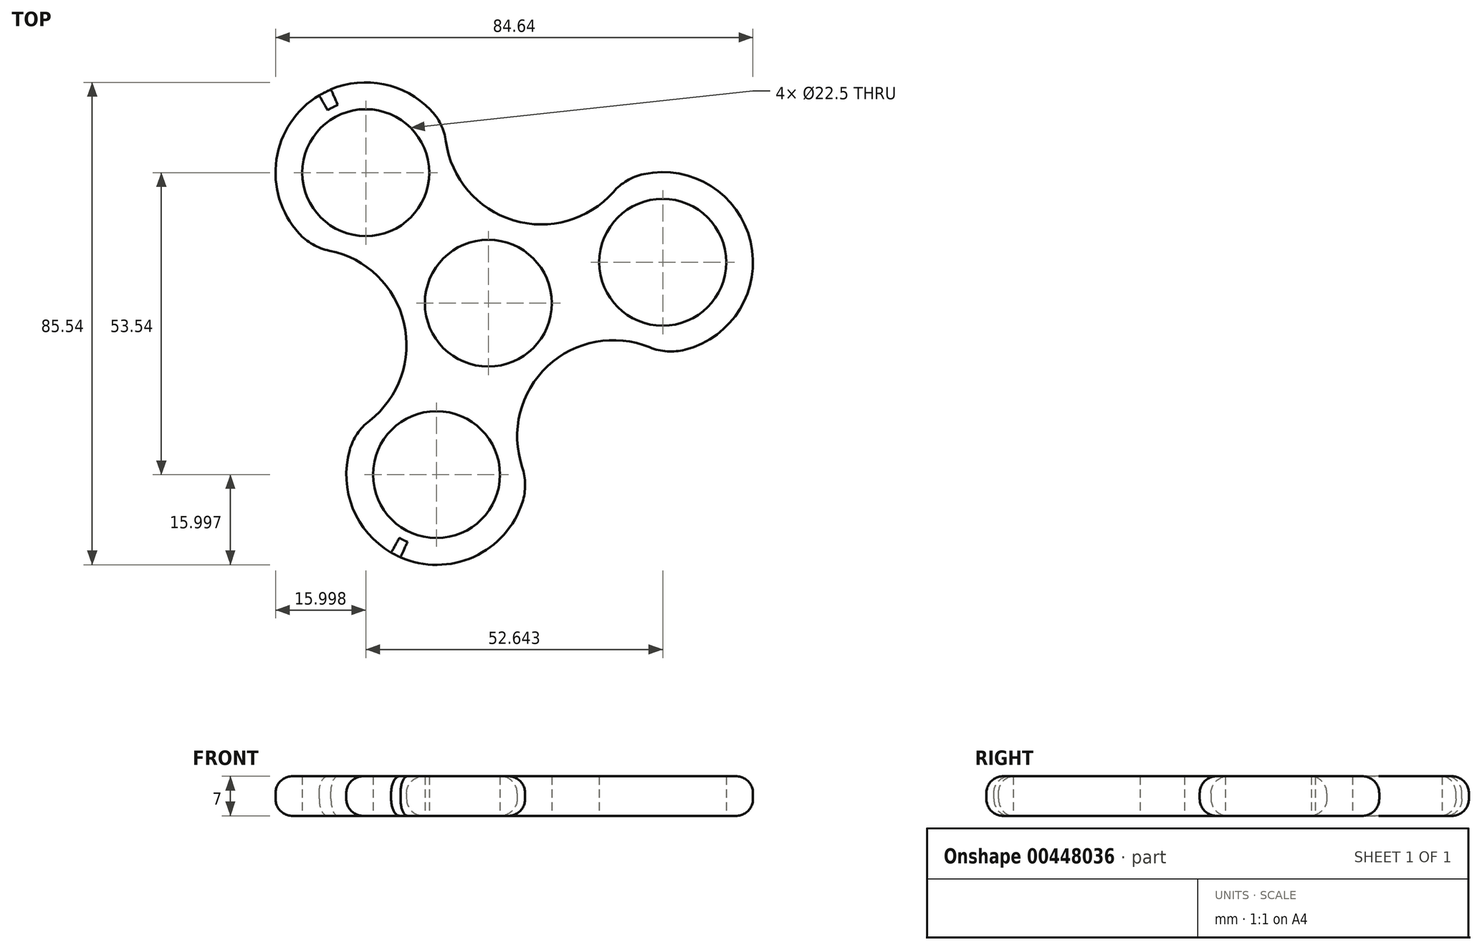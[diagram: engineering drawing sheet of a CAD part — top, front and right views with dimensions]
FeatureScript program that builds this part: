
annotation { "Feature Type Name" : "Feature", "Feature Type Description" : "" }
export const myFeature = defineFeature(function(context is Context, id is Id, definition is map)
    precondition{}
    {
        {
            var Q0;
            Q0=qCreatedBy(makeId("Top.planeOp"),FACE);
            var sketch = newSketch(context, id + "F0", { "sketchPlane" : qUnion([Q0])});
            skCircle(sketch, "E0", {"center": v(0, 0) * mm, "radius": 31.75 * mm});
            skCircle(sketch, "E1", {"center": v(30.91, 7.25) * mm, "radius": 16 * mm});
            skCircle(sketch, "E2", {"center": v(-21.73, 23.15) * mm, "radius": 16 * mm});
            skCircle(sketch, "E3", {"center": v(-9.18, -30.4) * mm, "radius": 16 * mm});
            skArc(sketch, "E4", {"start": v(-7.68, 30.8) * mm, "mid": v(4.44, 14.7) * mm, "end": v(23.45, 21.4) * mm});
            skArc(sketch, "E5", {"start": v(30.52, -8.75) * mm, "mid": v(10.5, -11.18) * mm, "end": v(6.8, -31.01) * mm});
            skArc(sketch, "E6", {"start": v(-22.84, -22.06) * mm, "mid": v(-14.95, -3.5) * mm, "end": v(-30.26, 9.6) * mm});
            skCircle(sketch, "E7", {"center": v(0, 0) * mm, "radius": 11.25 * mm});
            skCircle(sketch, "E8", {"center": v(30.91, 7.25) * mm, "radius": 11.25 * mm});
            skCircle(sketch, "E9", {"center": v(-21.73, 23.15) * mm, "radius": 11.25 * mm});
            skCircle(sketch, "E10", {"center": v(-9.18, -30.4) * mm, "radius": 11.25 * mm});
            skFitSpline(sketch, "E11", {"points": [v(46.91, 7.25) * mm, v(39.6, -18.54) * mm, v(30.52, -8.75) * mm], "startDerivative": vector(2, -70.39) * mm, "endDerivative": vector(-70.68, 26.23) * mm});
            skFitSpline(sketch, "E12", {"points": [v(-15.57, -45.06) * mm, v(-34.22, -24.14) * mm, v(-22.84, -22.06) * mm], "startDerivative": vector(-54.82, 25.3) * mm, "endDerivative": vector(33.4, 45.3) * mm});
            skFitSpline(sketch, "E13", {"points": [v(-29.99, 36.85) * mm, v(-4.27, 43.84) * mm, v(-7.68, 30.8) * mm], "startDerivative": vector(48.54, 26.45) * mm, "endDerivative": vector(14.14, -72.59) * mm});
            skSolve(sketch);
        }
        {
            var Q0;
            {var subQ0=sQuery(id+"F0.wireOp",EDGE,"E4");var subQ1=sQuery(id+"F0.wireOp",EDGE,"E2");var subQ4=makeQuery(id+"F0.imprint","INTERSECT",VERTEX,{"derivedFrom":[subQ1,subQ0]});Q0=makeQuery(id+"F0.imprint","IMPRINT",FACE,{"disambiguationData":[TD([[makeQuery(id+"F0.imprint","IMPRINT",EDGE,{"disambiguationData":[TD([[subQ4,1.0]])],"derivedFrom":subQ1}),1.0]])]});}
            var Q1;
            {var subQ1=sQuery(id+"F0.wireOp",EDGE,"E0");var subQ7=sQuery(id+"F0.wireOp",EDGE,"E9");var subQ9=makeQuery(id+"F0.imprint","INTERSECT",VERTEX,{"disambiguationData":[OD(0.0)],"derivedFrom":[subQ1,subQ7]});Q1=makeQuery(id+"F0.imprint","IMPRINT",FACE,{"disambiguationData":[TD([[makeQuery(id+"F0.imprint","IMPRINT",EDGE,{"disambiguationData":[TD([[subQ9,-1.0]])],"derivedFrom":subQ7}),-1.0]])]});}
            var Q2;
            Q2=makeQuery(id+"F0.imprint","IMPRINT",FACE,{"disambiguationData":[TD([[makeQuery(id+"F0.imprint","IMPRINT",EDGE,{"derivedFrom":sQuery(id+"F0.wireOp",EDGE,"E7")}),-1.0]])]});
            var Q3;
            {var subQ0=sQuery(id+"F0.wireOp",EDGE,"E5");var subQ1=sQuery(id+"F0.wireOp",EDGE,"E3");var subQ4=makeQuery(id+"F0.imprint","INTERSECT",VERTEX,{"derivedFrom":[subQ1,subQ0]});Q3=makeQuery(id+"F0.imprint","IMPRINT",FACE,{"disambiguationData":[TD([[makeQuery(id+"F0.imprint","IMPRINT",EDGE,{"disambiguationData":[TD([[subQ4,-1.0]])],"derivedFrom":subQ1}),1.0]])]});}
            var Q4;
            {var subQ1=sQuery(id+"F0.wireOp",EDGE,"E0");var subQ6=sQuery(id+"F0.wireOp",EDGE,"E10");var subQ7=makeQuery(id+"F0.imprint","INTERSECT",VERTEX,{"disambiguationData":[OD(0.0)],"derivedFrom":[subQ1,subQ6]});Q4=makeQuery(id+"F0.imprint","IMPRINT",FACE,{"disambiguationData":[TD([[makeQuery(id+"F0.imprint","IMPRINT",EDGE,{"disambiguationData":[TD([[subQ7,-1.0]])],"derivedFrom":subQ6}),-1.0]])]});}
            var Q5;
            {var subQ2=sQuery(id+"F0.wireOp",EDGE,"E0");var subQ6=sQuery(id+"F0.wireOp",EDGE,"E8");var subQ8=makeQuery(id+"F0.imprint","INTERSECT",VERTEX,{"disambiguationData":[OD(0.0)],"derivedFrom":[subQ2,subQ6]});Q5=makeQuery(id+"F0.imprint","IMPRINT",FACE,{"disambiguationData":[TD([[makeQuery(id+"F0.imprint","IMPRINT",EDGE,{"disambiguationData":[TD([[subQ8,1.0]])],"derivedFrom":subQ6}),-1.0]])]});}
            var Q6;
            {var subQ0=sQuery(id+"F0.wireOp",EDGE,"E4");var subQ1=sQuery(id+"F0.wireOp",EDGE,"E1");var subQ4=makeQuery(id+"F0.imprint","INTERSECT",VERTEX,{"derivedFrom":[subQ1,subQ0]});Q6=makeQuery(id+"F0.imprint","IMPRINT",FACE,{"disambiguationData":[TD([[makeQuery(id+"F0.imprint","IMPRINT",EDGE,{"disambiguationData":[TD([[subQ4,-1.0]])],"derivedFrom":subQ1}),1.0]])]});}
            var Q7;
            {var subQ0=sQuery(id+"F0.wireOp",EDGE,"ff2b849e-344e-4c15-b2b1-f3fe148f32d7");Q7=makeQuery(id+"F0.imprint","IMPRINT",FACE,{"disambiguationData":[TD([[makeQuery(id+"F0.imprint","IMPRINT",EDGE,{"derivedFrom":subQ0}),-1.0]])]});}
            var Q8;
            {var subQ0=sQuery(id+"F0.wireOp",EDGE,"E2");var subQ1=makeQuery(id+"F0.imprint","INTERSECT",VERTEX,{"disambiguationData":[OD(0.0)],"derivedFrom":[subQ0,sQuery(id+"F0.wireOp",EDGE,"E13")]});Q8=makeQuery(id+"F0.imprint","IMPRINT",FACE,{"disambiguationData":[TD([[makeQuery(id+"F0.imprint","IMPRINT",EDGE,{"disambiguationData":[TD([[subQ1,1.0]])],"derivedFrom":subQ0}),-1.0]])]});}
            var Q9;
            {var subQ0=sQuery(id+"F0.wireOp",EDGE,"E3");var subQ1=makeQuery(id+"F0.imprint","INTERSECT",VERTEX,{"disambiguationData":[OD(0.0)],"derivedFrom":[subQ0,sQuery(id+"F0.wireOp",EDGE,"E12")]});Q9=makeQuery(id+"F0.imprint","IMPRINT",FACE,{"disambiguationData":[TD([[makeQuery(id+"F0.imprint","IMPRINT",EDGE,{"disambiguationData":[TD([[subQ1,1.0]])],"derivedFrom":subQ0}),-1.0]])]});}
            var Q10;
            {var subQ0=sQuery(id+"F0.wireOp",EDGE,"0b5abbfc-5263-4152-91cc-4886121da727");var subQ1=sQuery(id+"F0.wireOp",EDGE,"E2");var subQ2=makeQuery(id+"F0.imprint","INTERSECT",VERTEX,{"disambiguationData":[OD(1.0)],"derivedFrom":[subQ1,subQ0]});Q10=makeQuery(id+"F0.imprint","IMPRINT",FACE,{"disambiguationData":[TD([[makeQuery(id+"F0.imprint","IMPRINT",EDGE,{"disambiguationData":[TD([[subQ2,-1.0]])],"derivedFrom":subQ1}),-1.0]])]});}
            var Q11;
            {var subQ0=sQuery(id+"F0.wireOp",EDGE,"0b5abbfc-5263-4152-91cc-4886121da727");var subQ1=sQuery(id+"F0.wireOp",EDGE,"E2");var subQ2=makeQuery(id+"F0.imprint","INTERSECT",VERTEX,{"disambiguationData":[OD(2.0)],"derivedFrom":[subQ1,subQ0]});Q11=makeQuery(id+"F0.imprint","IMPRINT",FACE,{"disambiguationData":[TD([[makeQuery(id+"F0.imprint","IMPRINT",EDGE,{"disambiguationData":[TD([[subQ2,-1.0]])],"derivedFrom":subQ1}),-1.0]])]});}
            extrude(context, id + "F1", {"entities" : qUnion([Q0, Q1, Q2, Q3, Q4, Q5, Q6, Q7, Q8, Q9, Q10, Q11]), "depth" : 7 * mm});
        }
        {
            var Q0;
            Q0=makeQuery(id+"F1.opExtrude","CAP_EDGE",EDGE,{"disambiguationData":[OSD([sQuery(id+"F0.wireOp",EDGE,"E5")])],"isStart":false});
            var Q1;
            Q1=makeQuery(id+"F1.opExtrude","CAP_EDGE",EDGE,{"disambiguationData":[OSD([sQuery(id+"F0.wireOp",EDGE,"E3")])],"isStart":false});
            var Q2;
            Q2=makeQuery(id+"F1.opExtrude","CAP_EDGE",EDGE,{"disambiguationData":[OSD([sQuery(id+"F0.wireOp",EDGE,"E12")])],"isStart":false});
            var Q3;
            Q3=makeQuery(id+"F1.opExtrude","CAP_EDGE",EDGE,{"disambiguationData":[OSD([sQuery(id+"F0.wireOp",EDGE,"E6")])],"isStart":false});
            var Q4;
            Q4=makeQuery(id+"F1.opExtrude","CAP_EDGE",EDGE,{"disambiguationData":[OSD([sQuery(id+"F0.wireOp",EDGE,"E2")])],"isStart":false});
            var Q5;
            Q5=makeQuery(id+"F1.opExtrude","CAP_EDGE",EDGE,{"disambiguationData":[OSD([sQuery(id+"F0.wireOp",EDGE,"E13")])],"isStart":false});
            var Q6;
            Q6=makeQuery(id+"F1.opExtrude","CAP_EDGE",EDGE,{"disambiguationData":[OSD([sQuery(id+"F0.wireOp",EDGE,"E4")])],"isStart":false});
            var Q7;
            Q7=makeQuery(id+"F1.opExtrude","CAP_EDGE",EDGE,{"disambiguationData":[OSD([sQuery(id+"F0.wireOp",EDGE,"E1")])],"isStart":false});
            var Q8;
            Q8=makeQuery(id+"F1.opExtrude","CAP_EDGE",EDGE,{"disambiguationData":[OSD([sQuery(id+"F0.wireOp",EDGE,"E11")])],"isStart":false});
            fillet(context, id + "F2", {"entities" : qUnion([Q0, Q1, Q2, Q3, Q4, Q5, Q6, Q7, Q8]), "radius" : 3 * mm, "tangentPropagation" : true, "allowEdgeOverflow" : false});
        }
        {
            var Q0;
            Q0=makeQuery(id+"F1.opExtrude","CAP_EDGE",EDGE,{"disambiguationData":[OSD([sQuery(id+"F0.wireOp",EDGE,"E3")])],"isStart":true});
            var Q1;
            Q1=makeQuery(id+"F1.opExtrude","CAP_EDGE",EDGE,{"disambiguationData":[OSD([sQuery(id+"F0.wireOp",EDGE,"E12")])],"isStart":true});
            var Q2;
            Q2=makeQuery(id+"F1.opExtrude","CAP_EDGE",EDGE,{"disambiguationData":[OSD([sQuery(id+"F0.wireOp",EDGE,"E6")])],"isStart":true});
            var Q3;
            Q3=makeQuery(id+"F1.opExtrude","CAP_EDGE",EDGE,{"disambiguationData":[OSD([sQuery(id+"F0.wireOp",EDGE,"E2")])],"isStart":true});
            var Q4;
            Q4=makeQuery(id+"F1.opExtrude","CAP_EDGE",EDGE,{"disambiguationData":[OSD([sQuery(id+"F0.wireOp",EDGE,"E13")])],"isStart":true});
            var Q5;
            Q5=makeQuery(id+"F1.opExtrude","CAP_EDGE",EDGE,{"disambiguationData":[OSD([sQuery(id+"F0.wireOp",EDGE,"E4")])],"isStart":true});
            var Q6;
            Q6=makeQuery(id+"F1.opExtrude","CAP_EDGE",EDGE,{"disambiguationData":[OSD([sQuery(id+"F0.wireOp",EDGE,"E1")])],"isStart":true});
            var Q7;
            Q7=makeQuery(id+"F1.opExtrude","CAP_EDGE",EDGE,{"disambiguationData":[OSD([sQuery(id+"F0.wireOp",EDGE,"E11")])],"isStart":true});
            var Q8;
            Q8=makeQuery(id+"F1.opExtrude","CAP_EDGE",EDGE,{"disambiguationData":[OSD([sQuery(id+"F0.wireOp",EDGE,"E5")])],"isStart":true});
            fillet(context, id + "F3", {"entities" : qUnion([Q0, Q1, Q2, Q3, Q4, Q5, Q6, Q7, Q8]), "radius" : 3 * mm, "tangentPropagation" : true, "allowEdgeOverflow" : false});
        }
        {
            var Q0;
            {var subQ0=sQuery(id+"F0.wireOp",EDGE,"E6");var subQ1=sQuery(id+"F0.wireOp",EDGE,"E2");Q0=makeQuery(id+"F2.opFillet","BLEND_EDGE",EDGE,{"blendedFrom":[makeQuery(id+"F1.opExtrude","CAP_EDGE",EDGE,{"disambiguationData":[OSD([subQ1]),TDD([makeQuery(id+"F0.imprint","IMPRINT",EDGE,{"disambiguationData":[TD([[makeQuery(id+"F0.imprint","INTERSECT",VERTEX,{"disambiguationData":[OD(0.0)],"derivedFrom":[subQ1,sQuery(id+"F0.wireOp",EDGE,"E13")]}),-1.0]])],"derivedFrom":subQ1})])],"isStart":false}),makeQuery(id+"F1.opExtrude","CAP_EDGE",EDGE,{"disambiguationData":[OSD([subQ0])],"isStart":false})],"blendedInto":[]});}
            var Q1;
            {var subQ0=sQuery(id+"F0.wireOp",EDGE,"E6");var subQ1=sQuery(id+"F0.wireOp",EDGE,"E2");Q1=makeQuery(id+"F3.opFillet","BLEND_EDGE",EDGE,{"blendedFrom":[makeQuery(id+"F1.opExtrude","CAP_EDGE",EDGE,{"disambiguationData":[OSD([subQ1]),TDD([makeQuery(id+"F0.imprint","IMPRINT",EDGE,{"disambiguationData":[TD([[makeQuery(id+"F0.imprint","INTERSECT",VERTEX,{"disambiguationData":[OD(0.0)],"derivedFrom":[subQ1,sQuery(id+"F0.wireOp",EDGE,"E13")]}),-1.0]])],"derivedFrom":subQ1})])],"isStart":true}),makeQuery(id+"F1.opExtrude","CAP_EDGE",EDGE,{"disambiguationData":[OSD([subQ0])],"isStart":true})],"blendedInto":[]});}
            var Q2;
            Q2=makeQuery(id+"F1.opExtrude","SWEPT_EDGE",EDGE,{"disambiguationData":[OSD([sQuery(id+"F0.wireOp",EDGE,"E0"),sQuery(id+"F0.wireOp",EDGE,"E2"),sQuery(id+"F0.wireOp",EDGE,"E6")])]});
            var Q3;
            {var subQ0=sQuery(id+"F0.wireOp",EDGE,"E4");var subQ1=sQuery(id+"F0.wireOp",EDGE,"E13");var subQ2=sQuery(id+"F0.wireOp",EDGE,"E2");Q3=makeQuery(id+"F2.opFillet","BLEND_EDGE",EDGE,{"blendedFrom":[makeQuery(id+"F1.opExtrude","CAP_EDGE",EDGE,{"disambiguationData":[OSD([subQ2]),TDD([makeQuery(id+"F0.imprint","IMPRINT",EDGE,{"disambiguationData":[TD([[makeQuery(id+"F0.imprint","INTERSECT",VERTEX,{"disambiguationData":[OD(1.0)],"derivedFrom":[subQ2,subQ1]}),1.0]])],"derivedFrom":subQ2})])],"isStart":false}),makeQuery(id+"F1.opExtrude","CAP_EDGE",EDGE,{"disambiguationData":[OSD([subQ0])],"isStart":false})],"blendedInto":[]});}
            var Q4;
            Q4=makeQuery(id+"F1.opExtrude","SWEPT_EDGE",EDGE,{"disambiguationData":[OSD([sQuery(id+"F0.wireOp",EDGE,"E0"),sQuery(id+"F0.wireOp",EDGE,"E2"),sQuery(id+"F0.wireOp",EDGE,"E4"),sQuery(id+"F0.wireOp",EDGE,"E13")])]});
            var Q5;
            {var subQ0=sQuery(id+"F0.wireOp",EDGE,"E4");var subQ1=sQuery(id+"F0.wireOp",EDGE,"E13");var subQ2=sQuery(id+"F0.wireOp",EDGE,"E2");Q5=makeQuery(id+"F3.opFillet","BLEND_EDGE",EDGE,{"blendedFrom":[makeQuery(id+"F1.opExtrude","CAP_EDGE",EDGE,{"disambiguationData":[OSD([subQ2]),TDD([makeQuery(id+"F0.imprint","IMPRINT",EDGE,{"disambiguationData":[TD([[makeQuery(id+"F0.imprint","INTERSECT",VERTEX,{"disambiguationData":[OD(1.0)],"derivedFrom":[subQ2,subQ1]}),1.0]])],"derivedFrom":subQ2})])],"isStart":true}),makeQuery(id+"F1.opExtrude","CAP_EDGE",EDGE,{"disambiguationData":[OSD([subQ0])],"isStart":true})],"blendedInto":[]});}
            var Q6;
            {var subQ0=sQuery(id+"F0.wireOp",EDGE,"E6");var subQ1=sQuery(id+"F0.wireOp",EDGE,"E12");var subQ2=sQuery(id+"F0.wireOp",EDGE,"E3");Q6=makeQuery(id+"F3.opFillet","BLEND_EDGE",EDGE,{"blendedFrom":[makeQuery(id+"F1.opExtrude","CAP_EDGE",EDGE,{"disambiguationData":[OSD([subQ2]),TDD([makeQuery(id+"F0.imprint","IMPRINT",EDGE,{"disambiguationData":[TD([[makeQuery(id+"F0.imprint","INTERSECT",VERTEX,{"disambiguationData":[OD(1.0)],"derivedFrom":[subQ2,subQ1]}),1.0]])],"derivedFrom":subQ2})])],"isStart":true}),makeQuery(id+"F1.opExtrude","CAP_EDGE",EDGE,{"disambiguationData":[OSD([subQ0])],"isStart":true})],"blendedInto":[]});}
            var Q7;
            Q7=makeQuery(id+"F1.opExtrude","SWEPT_EDGE",EDGE,{"disambiguationData":[OSD([sQuery(id+"F0.wireOp",EDGE,"E0"),sQuery(id+"F0.wireOp",EDGE,"E3"),sQuery(id+"F0.wireOp",EDGE,"E6"),sQuery(id+"F0.wireOp",EDGE,"E12")])]});
            var Q8;
            {var subQ0=sQuery(id+"F0.wireOp",EDGE,"E6");var subQ1=sQuery(id+"F0.wireOp",EDGE,"E12");var subQ2=sQuery(id+"F0.wireOp",EDGE,"E3");Q8=makeQuery(id+"F2.opFillet","BLEND_EDGE",EDGE,{"blendedFrom":[makeQuery(id+"F1.opExtrude","CAP_EDGE",EDGE,{"disambiguationData":[OSD([subQ2]),TDD([makeQuery(id+"F0.imprint","IMPRINT",EDGE,{"disambiguationData":[TD([[makeQuery(id+"F0.imprint","INTERSECT",VERTEX,{"disambiguationData":[OD(1.0)],"derivedFrom":[subQ2,subQ1]}),1.0]])],"derivedFrom":subQ2})])],"isStart":false}),makeQuery(id+"F1.opExtrude","CAP_EDGE",EDGE,{"disambiguationData":[OSD([subQ0])],"isStart":false})],"blendedInto":[]});}
            var Q9;
            {var subQ0=sQuery(id+"F0.wireOp",EDGE,"E5");var subQ1=sQuery(id+"F0.wireOp",EDGE,"E3");Q9=makeQuery(id+"F2.opFillet","BLEND_EDGE",EDGE,{"blendedFrom":[makeQuery(id+"F1.opExtrude","CAP_EDGE",EDGE,{"disambiguationData":[OSD([subQ1]),TDD([makeQuery(id+"F0.imprint","IMPRINT",EDGE,{"disambiguationData":[TD([[makeQuery(id+"F0.imprint","INTERSECT",VERTEX,{"disambiguationData":[OD(0.0)],"derivedFrom":[subQ1,sQuery(id+"F0.wireOp",EDGE,"E12")]}),-1.0]])],"derivedFrom":subQ1})])],"isStart":false}),makeQuery(id+"F1.opExtrude","CAP_EDGE",EDGE,{"disambiguationData":[OSD([subQ0])],"isStart":false})],"blendedInto":[]});}
            var Q10;
            Q10=makeQuery(id+"F1.opExtrude","SWEPT_EDGE",EDGE,{"disambiguationData":[OSD([sQuery(id+"F0.wireOp",EDGE,"E0"),sQuery(id+"F0.wireOp",EDGE,"E3"),sQuery(id+"F0.wireOp",EDGE,"E5")])]});
            var Q11;
            {var subQ0=sQuery(id+"F0.wireOp",EDGE,"E5");var subQ1=sQuery(id+"F0.wireOp",EDGE,"E3");Q11=makeQuery(id+"F3.opFillet","BLEND_EDGE",EDGE,{"blendedFrom":[makeQuery(id+"F1.opExtrude","CAP_EDGE",EDGE,{"disambiguationData":[OSD([subQ1]),TDD([makeQuery(id+"F0.imprint","IMPRINT",EDGE,{"disambiguationData":[TD([[makeQuery(id+"F0.imprint","INTERSECT",VERTEX,{"disambiguationData":[OD(0.0)],"derivedFrom":[subQ1,sQuery(id+"F0.wireOp",EDGE,"E12")]}),-1.0]])],"derivedFrom":subQ1})])],"isStart":true}),makeQuery(id+"F1.opExtrude","CAP_EDGE",EDGE,{"disambiguationData":[OSD([subQ0])],"isStart":true})],"blendedInto":[]});}
            var Q12;
            Q12=makeQuery(id+"F2.opFillet","BLEND_EDGE",EDGE,{"blendedFrom":[makeQuery(id+"F1.opExtrude","CAP_EDGE",EDGE,{"disambiguationData":[OSD([sQuery(id+"F0.wireOp",EDGE,"E1")])],"isStart":false}),makeQuery(id+"F1.opExtrude","CAP_EDGE",EDGE,{"disambiguationData":[OSD([sQuery(id+"F0.wireOp",EDGE,"E5")])],"isStart":false})],"blendedInto":[]});
            var Q13;
            Q13=makeQuery(id+"F1.opExtrude","SWEPT_EDGE",EDGE,{"disambiguationData":[OSD([sQuery(id+"F0.wireOp",EDGE,"E0"),sQuery(id+"F0.wireOp",EDGE,"E1"),sQuery(id+"F0.wireOp",EDGE,"E5"),sQuery(id+"F0.wireOp",EDGE,"E11")])]});
            var Q14;
            Q14=makeQuery(id+"F3.opFillet","BLEND_EDGE",EDGE,{"blendedFrom":[makeQuery(id+"F1.opExtrude","CAP_EDGE",EDGE,{"disambiguationData":[OSD([sQuery(id+"F0.wireOp",EDGE,"E1")])],"isStart":true}),makeQuery(id+"F1.opExtrude","CAP_EDGE",EDGE,{"disambiguationData":[OSD([sQuery(id+"F0.wireOp",EDGE,"E5")])],"isStart":true})],"blendedInto":[]});
            var Q15;
            Q15=makeQuery(id+"F1.opExtrude","SWEPT_EDGE",EDGE,{"disambiguationData":[OSD([sQuery(id+"F0.wireOp",EDGE,"E0"),sQuery(id+"F0.wireOp",EDGE,"E1"),sQuery(id+"F0.wireOp",EDGE,"E4")])]});
            var Q16;
            Q16=makeQuery(id+"F2.opFillet","BLEND_EDGE",EDGE,{"blendedFrom":[makeQuery(id+"F1.opExtrude","CAP_EDGE",EDGE,{"disambiguationData":[OSD([sQuery(id+"F0.wireOp",EDGE,"E1")])],"isStart":false}),makeQuery(id+"F1.opExtrude","CAP_EDGE",EDGE,{"disambiguationData":[OSD([sQuery(id+"F0.wireOp",EDGE,"E4")])],"isStart":false})],"blendedInto":[]});
            var Q17;
            Q17=makeQuery(id+"F3.opFillet","BLEND_EDGE",EDGE,{"blendedFrom":[makeQuery(id+"F1.opExtrude","CAP_EDGE",EDGE,{"disambiguationData":[OSD([sQuery(id+"F0.wireOp",EDGE,"E1")])],"isStart":true}),makeQuery(id+"F1.opExtrude","CAP_EDGE",EDGE,{"disambiguationData":[OSD([sQuery(id+"F0.wireOp",EDGE,"E4")])],"isStart":true})],"blendedInto":[]});
            fillet(context, id + "F4", {"entities" : qUnion([Q0, Q1, Q2, Q3, Q4, Q5, Q6, Q7, Q8, Q9, Q10, Q11, Q12, Q13, Q14, Q15, Q16, Q17]), "radius" : 10 * mm, "tangentPropagation" : true, "allowEdgeOverflow" : false});
        }
    });
